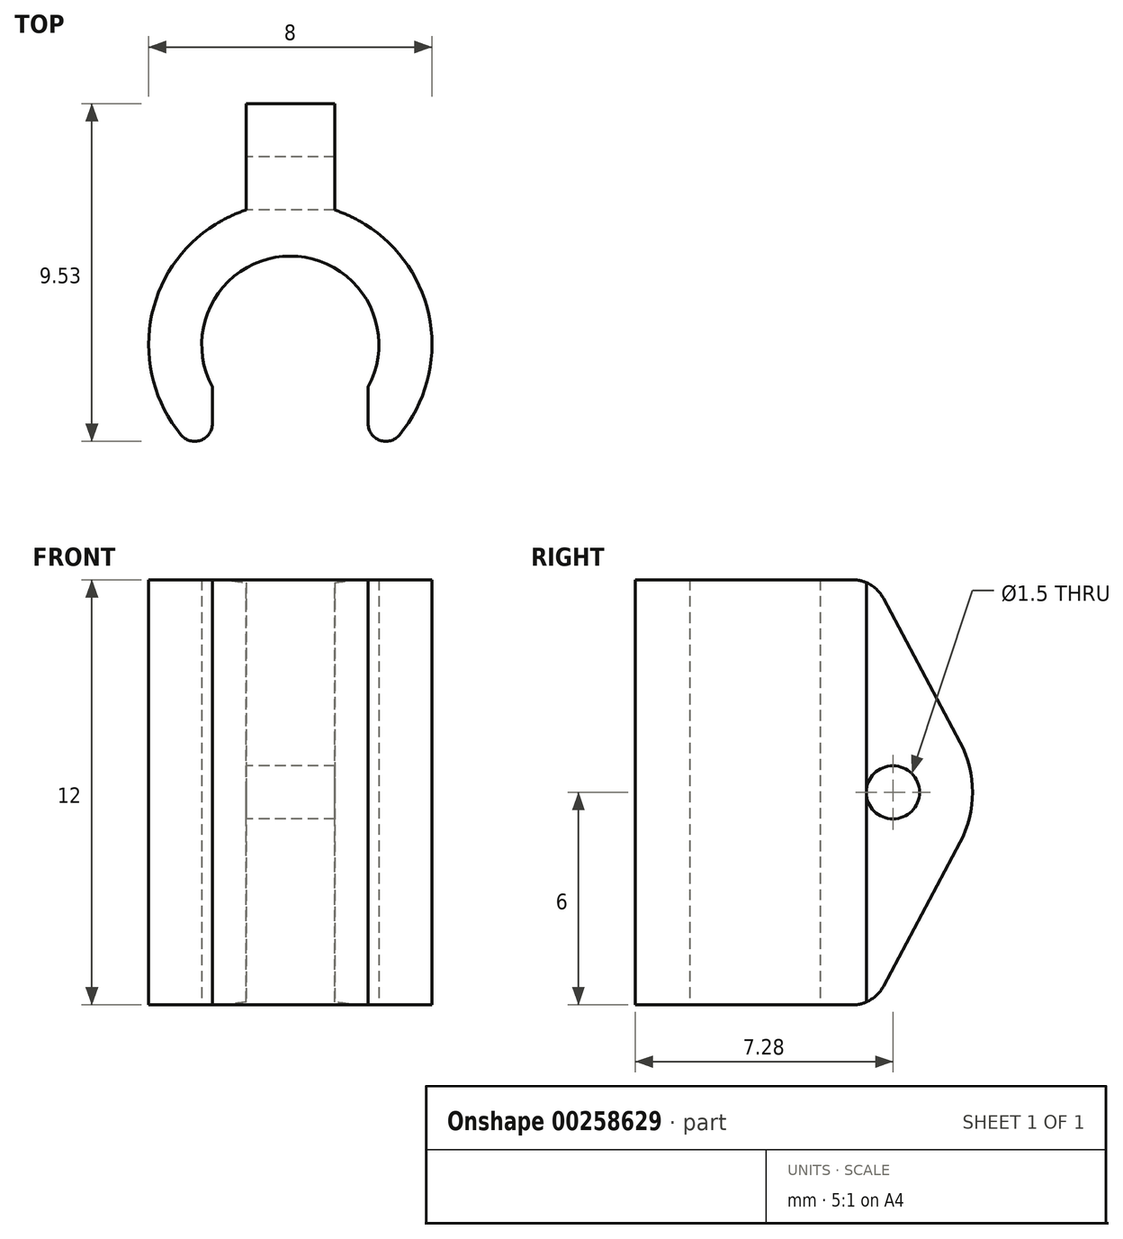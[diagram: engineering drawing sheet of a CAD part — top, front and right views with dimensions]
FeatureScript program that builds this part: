
annotation { "Feature Type Name" : "Feature", "Feature Type Description" : "" }
export const myFeature = defineFeature(function(context is Context, id is Id, definition is map)
    precondition{}
    {
        {
            var Q0;
            Q0=qCreatedBy(makeId("Top.planeOp"),FACE);
            var sketch = newSketch(context, id + "F0", { "sketchPlane" : qUnion([Q0])});
            skArc(sketch, "E0", {"start": v(2.2, -1.19) * mm, "mid": v(0, 2.5) * mm, "end": v(-2.2, -1.19) * mm});
            skArc(sketch, "E1", {"start": v(3.09, -2.55) * mm, "mid": v(0, 4) * mm, "end": v(-3.09, -2.55) * mm});
            skLineSegment(sketch, "E2.left", {"start": v(-2.2, -1.19) * mm, "end": v(-2.2, -2.23) * mm});
            skLineSegment(sketch, "E2.right", {"start": v(2.2, -1.19) * mm, "end": v(2.2, -2.23) * mm});
            skLineSegment(sketch, "E3", {"start": v(-2.2, -2.26) * mm, "end": v(2.2, -2.26) * mm, "construction": true});
            skPoint(sketch, "E4.visualSharp", {"position": v(-2.2, -3.34) * mm});
            skArc(sketch, "E4.filletArc", {"start": v(-3.09, -2.55) * mm, "mid": v(-2.53, -2.7) * mm, "end": v(-2.2, -2.23) * mm});
            skPoint(sketch, "E5.visualSharp", {"position": v(2.2, -3.34) * mm});
            skArc(sketch, "E5.filletArc", {"start": v(2.2, -2.23) * mm, "mid": v(2.53, -2.7) * mm, "end": v(3.09, -2.55) * mm});
            skSolve(sketch);
        }
        {
            var Q0;
            Q0=makeQuery(id+"F0.imprint","IMPRINT",FACE,{"disambiguationData":[TD([[makeQuery(id+"F0.imprint","IMPRINT",EDGE,{"derivedFrom":sQuery(id+"F0.wireOp",EDGE,"E0")}),-1.0]])]});
            extrude(context, id + "F1", {"entities" : qUnion([Q0]), "depth" : 12 * mm});
        }
        {
            var Q0;
            Q0=qCreatedBy(makeId("Right.planeOp"),FACE);
            var sketch = newSketch(context, id + "F2", { "sketchPlane" : qUnion([Q0])});
            skLineSegment(sketch, "E6", {"start": v(4, 0) * mm, "end": v(6.45, 4.59) * mm});
            skLineSegment(sketch, "E7", {"start": v(6.45, 7.41) * mm, "end": v(4, 12) * mm});
            skLineSegment(sketch, "E8", {"start": v(2.5, 6) * mm, "end": v(7.2, 6) * mm, "construction": true});
            skPoint(sketch, "E9.visualSharp", {"position": v(7.2, 6) * mm});
            skArc(sketch, "E9.filletArc", {"start": v(6.45, 4.59) * mm, "mid": v(6.8, 6) * mm, "end": v(6.45, 7.41) * mm});
            skLineSegment(sketch, "E10", {"start": v(4, 12) * mm, "end": v(2.5, 12) * mm});
            skLineSegment(sketch, "E11", {"start": v(2.5, 12) * mm, "end": v(2.5, 0) * mm});
            skLineSegment(sketch, "E12", {"start": v(2.5, 0) * mm, "end": v(4, 0) * mm});
            skSolve(sketch);
        }
        {
            var Q0;
            Q0=makeQuery(id+"F2.imprint","IMPRINT",FACE,{"disambiguationData":[TD([[makeQuery(id+"F2.imprint","IMPRINT",EDGE,{"derivedFrom":sQuery(id+"F2.wireOp",EDGE,"E6")}),1.0]])]});
            extrude(context, id + "F3", {"entities" : qUnion([Q0]), "operationType" : NewBodyOperationType.ADD, "endBound" : BoundingType.SYMMETRIC, "depth" : 2.5 * mm});
        }
        {
            var Q0;
            Q0=makeQuery(id+"F3.opExtrude","SWEPT_EDGE",EDGE,{"disambiguationData":[OSD([sQuery(id+"F2.wireOp",EDGE,"E7"),sQuery(id+"F2.wireOp",EDGE,"E10")])]});
            var Q1;
            Q1=makeQuery(id+"F3.opExtrude","SWEPT_EDGE",EDGE,{"disambiguationData":[OSD([sQuery(id+"F2.wireOp",EDGE,"E6"),sQuery(id+"F2.wireOp",EDGE,"E12")])]});
            fillet(context, id + "F4", {"entities" : qUnion([Q0, Q1]), "radius" : 1 * mm, "tangentPropagation" : true, "allowEdgeOverflow" : false});
        }
        {
            var Q0;
            Q0=makeQuery(id+"F3.opExtrude","CAP_FACE",FACE,{"disambiguationData":[OSD([sQuery(id+"F2.wireOp",EDGE,"E6"),sQuery(id+"F2.wireOp",EDGE,"E7"),sQuery(id+"F2.wireOp",EDGE,"E9.filletArc"),sQuery(id+"F2.wireOp",EDGE,"E10"),sQuery(id+"F2.wireOp",EDGE,"E11"),sQuery(id+"F2.wireOp",EDGE,"E12")])],"isStart":true});
            var sketch = newSketch(context, id + "F5", { "sketchPlane" : qUnion([Q0])});
            skCircle(sketch, "E13", {"center": v(-4.55, 6) * mm, "radius": 0.75 * mm});
            skSolve(sketch);
        }
        {
            var Q0;
            Q0=makeQuery(id+"F5.imprint","IMPRINT",FACE,{"disambiguationData":[TD([[makeQuery(id+"F5.imprint","IMPRINT",EDGE,{"derivedFrom":sQuery(id+"F5.wireOp",EDGE,"E13")}),1.0]])]});
            extrude(context, id + "F6", {"entities" : qUnion([Q0]), "operationType" : NewBodyOperationType.REMOVE, "endBound" : BoundingType.UP_TO_NEXT, "oppositeDirection" : true, "depth" : 25 * mm});
        }
    });
